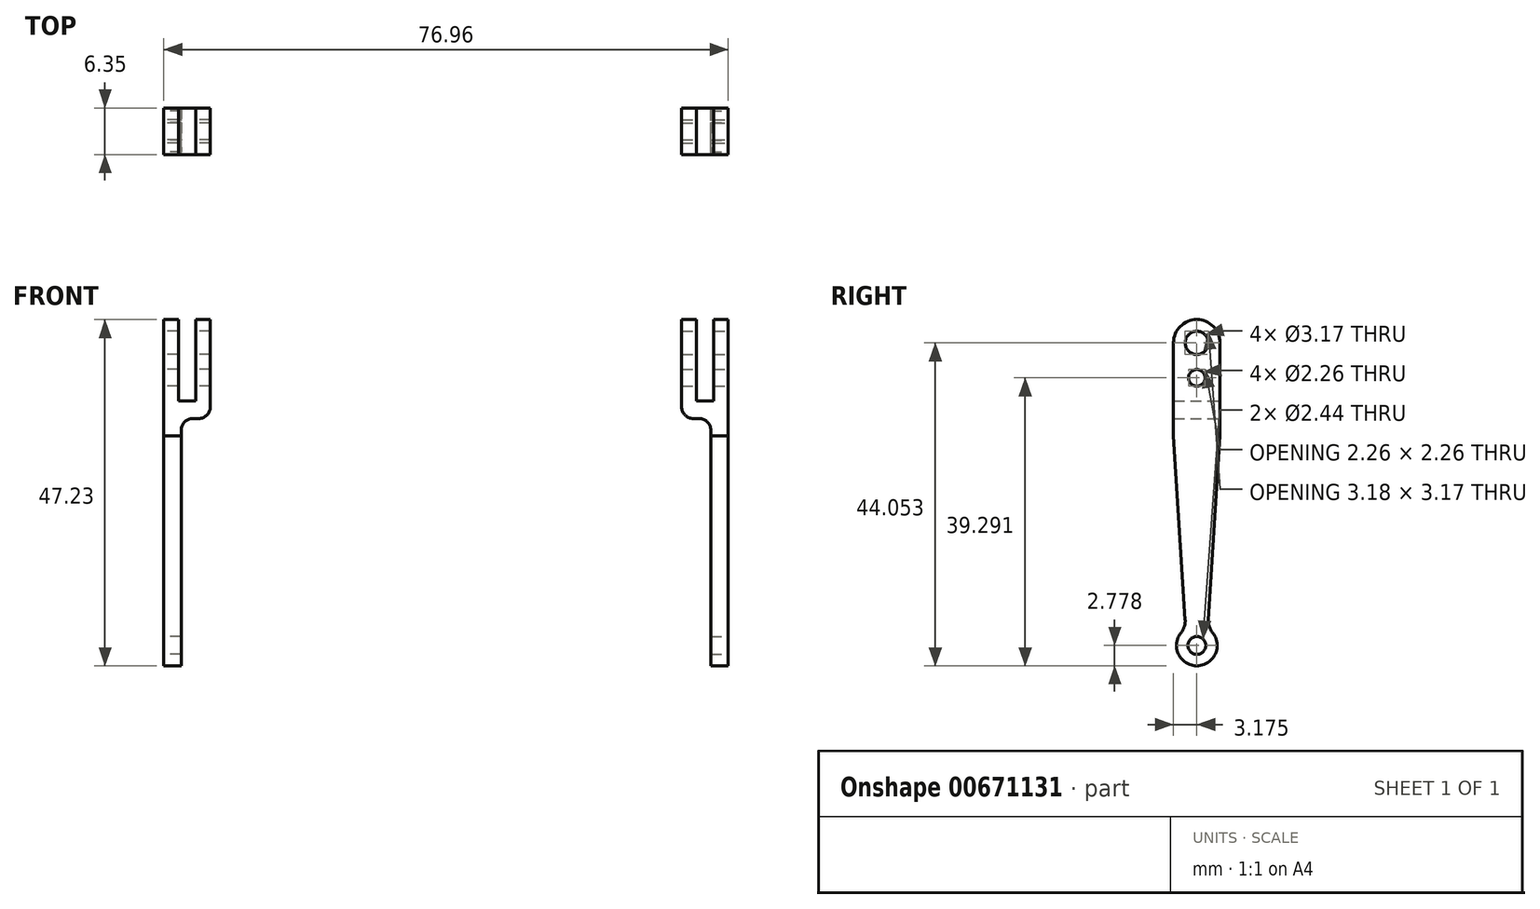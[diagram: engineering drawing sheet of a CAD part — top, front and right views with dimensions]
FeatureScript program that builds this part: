
annotation { "Feature Type Name" : "Feature", "Feature Type Description" : "" }
export const myFeature = defineFeature(function(context is Context, id is Id, definition is map)
    precondition{}
    {
        {
            var Q0;
            Q0=qCreatedBy(makeId("Front.planeOp"),FACE);
            var sketch = newSketch(context, id + "F0", { "sketchPlane" : qUnion([Q0])});
            skLineSegment(sketch, "E0", {"start": v(38.48, 4.76) * mm, "end": v(38.48, 51.99) * mm});
            skLineSegment(sketch, "E1", {"start": v(38.48, 51.99) * mm, "end": v(36.5, 51.99) * mm});
            skLineSegment(sketch, "E2", {"start": v(36.5, 51.99) * mm, "end": v(36.5, 40.88) * mm});
            skLineSegment(sketch, "E3", {"start": v(36.5, 40.88) * mm, "end": v(34.12, 40.88) * mm});
            skLineSegment(sketch, "E4", {"start": v(34.12, 40.88) * mm, "end": v(34.12, 51.99) * mm});
            skLineSegment(sketch, "E5", {"start": v(34.12, 51.99) * mm, "end": v(32.13, 51.99) * mm});
            skLineSegment(sketch, "E6", {"start": v(32.13, 51.99) * mm, "end": v(32.13, 38.5) * mm});
            skLineSegment(sketch, "E7", {"start": v(32.13, 38.5) * mm, "end": v(36.1, 38.5) * mm});
            skLineSegment(sketch, "E8", {"start": v(36.1, 38.5) * mm, "end": v(36.1, 4.76) * mm});
            skLineSegment(sketch, "E9", {"start": v(36.1, 4.76) * mm, "end": v(38.48, 4.76) * mm});
            skSolve(sketch);
        }
        {
            var Q0;
            Q0=qSketchRegion(id+"F0",true);
            extrude(context, id + "F1", {"entities" : qUnion([Q0]), "depth" : 6.35 * mm});
        }
        {
            var Q0;
            Q0=makeQuery(id+"F1.opExtrude","SWEPT_EDGE",EDGE,{"disambiguationData":[OSD([sQuery(id+"F0.wireOp",EDGE,"E7"),sQuery(id+"F0.wireOp",EDGE,"E8")])]});
            var Q1;
            Q1=makeQuery(id+"F1.opExtrude","SWEPT_EDGE",EDGE,{"disambiguationData":[OSD([sQuery(id+"F0.wireOp",EDGE,"E6"),sQuery(id+"F0.wireOp",EDGE,"E7")])]});
            fillet(context, id + "F2", {"entities" : qUnion([Q0, Q1]), "radius" : 1.59 * mm, "tangentPropagation" : true, "allowEdgeOverflow" : false});
        }
        {
            var Q0;
            Q0=makeQuery(id+"F1.opExtrude","CAP_EDGE",EDGE,{"disambiguationData":[OSD([sQuery(id+"F0.wireOp",EDGE,"E5")])],"isStart":false});
            var Q1;
            Q1=makeQuery(id+"F1.opExtrude","CAP_EDGE",EDGE,{"disambiguationData":[OSD([sQuery(id+"F0.wireOp",EDGE,"E5")])],"isStart":true});
            var Q2;
            Q2=makeQuery(id+"F1.opExtrude","CAP_EDGE",EDGE,{"disambiguationData":[OSD([sQuery(id+"F0.wireOp",EDGE,"E1")])],"isStart":true});
            var Q3;
            Q3=makeQuery(id+"F1.opExtrude","CAP_EDGE",EDGE,{"disambiguationData":[OSD([sQuery(id+"F0.wireOp",EDGE,"E1")])],"isStart":false});
            fillet(context, id + "F3", {"entities" : qUnion([Q0, Q1, Q2, Q3]), "radius" : 3.17 * mm, "tangentPropagation" : true, "allowEdgeOverflow" : false});
        }
        {
            var Q0;
            Q0=makeQuery(id+"F1.opExtrude","SWEPT_FACE",FACE,{"disambiguationData":[OSD([sQuery(id+"F0.wireOp",EDGE,"E0")])]});
            var sketch = newSketch(context, id + "F4", { "sketchPlane" : qUnion([Q0])});
            skPoint(sketch, "E10", {"position": v(-3.18, 48.81) * mm});
            skPoint(sketch, "E11", {"position": v(-3.18, 44.05) * mm});
            skSolve(sketch);
        }
        {
            var Q0;
            Q0=sQuery(id+"F4.wireOp",VERTEX,"E10");
            var Q1;
            Q1=makeQuery(id+"F1.opExtrude","SWEPT_BODY",BODY,{"disambiguationData":[OSD([sQuery(id+"F0.wireOp",EDGE,"E0"),sQuery(id+"F0.wireOp",EDGE,"E1"),sQuery(id+"F0.wireOp",EDGE,"E2"),sQuery(id+"F0.wireOp",EDGE,"E3"),sQuery(id+"F0.wireOp",EDGE,"E4"),sQuery(id+"F0.wireOp",EDGE,"E5"),sQuery(id+"F0.wireOp",EDGE,"E6"),sQuery(id+"F0.wireOp",EDGE,"E7"),sQuery(id+"F0.wireOp",EDGE,"E8"),sQuery(id+"F0.wireOp",EDGE,"E9")])]});
            hole(context, id + "F5", {"style" : HoleStyle.SIMPLE, "endStyle" : HoleEndStyle.THROUGH, "holeDiameter" : 3.17 * mm, "tappedDepth" : 12.7 * mm, "tapClearance" : 3, "locations" : qUnion([Q0]), "scope" : qUnion([Q1])});
        }
        {
            var Q0;
            Q0=makeQuery(id+"F1.opExtrude","SWEPT_FACE",FACE,{"disambiguationData":[OSD([sQuery(id+"F0.wireOp",EDGE,"E0")])]});
            var sketch = newSketch(context, id + "F6", { "sketchPlane" : qUnion([Q0])});
            skPoint(sketch, "E12", {"position": v(-3.18, 44.05) * mm});
            skSolve(sketch);
        }
        {
            var Q0;
            Q0=sQuery(id+"F6.wireOp",VERTEX,"E12");
            var Q1;
            Q1=makeQuery(id+"F1.opExtrude","SWEPT_BODY",BODY,{"disambiguationData":[OSD([sQuery(id+"F0.wireOp",EDGE,"E0"),sQuery(id+"F0.wireOp",EDGE,"E1"),sQuery(id+"F0.wireOp",EDGE,"E2"),sQuery(id+"F0.wireOp",EDGE,"E3"),sQuery(id+"F0.wireOp",EDGE,"E4"),sQuery(id+"F0.wireOp",EDGE,"E5"),sQuery(id+"F0.wireOp",EDGE,"E6"),sQuery(id+"F0.wireOp",EDGE,"E7"),sQuery(id+"F0.wireOp",EDGE,"E8"),sQuery(id+"F0.wireOp",EDGE,"E9")])]});
            hole(context, id + "F7", {"style" : HoleStyle.SIMPLE, "endStyle" : HoleEndStyle.THROUGH, "holeDiameter" : 2.26 * mm, "tappedDepth" : 12.7 * mm, "tapClearance" : 3, "locations" : qUnion([Q0]), "scope" : qUnion([Q1])});
        }
        {
            var Q0;
            Q0=makeQuery(id+"F1.opExtrude","SWEPT_FACE",FACE,{"disambiguationData":[OSD([sQuery(id+"F0.wireOp",EDGE,"E0")])]});
            var sketch = newSketch(context, id + "F8", { "sketchPlane" : qUnion([Q0])});
            skCircle(sketch, "E13", {"center": v(-3.18, 7.54) * mm, "radius": 1.22 * mm});
            skCircle(sketch, "E14", {"center": v(-3.18, 7.54) * mm, "radius": 2.78 * mm});
            skLineSegment(sketch, "E15", {"start": v(-6.35, 36.11) * mm, "end": v(0, 36.11) * mm});
            skLineSegment(sketch, "E16", {"start": v(-6.35, 11.06) * mm, "end": v(0, 11.06) * mm});
            skLineSegment(sketch, "E17", {"start": v(-6.35, 36.11) * mm, "end": v(-4.76, 11.06) * mm});
            skLineSegment(sketch, "E18", {"start": v(0, 36.11) * mm, "end": v(-1.59, 11.06) * mm});
            skArc(sketch, "E19", {"start": v(-5.33, 9.3) * mm, "mid": v(-4.88, 10.12) * mm, "end": v(-4.76, 11.06) * mm});
            skArc(sketch, "E20", {"start": v(-1.59, 11.06) * mm, "mid": v(-1.47, 10.12) * mm, "end": v(-1.02, 9.3) * mm});
            skSolve(sketch);
        }
        {
            var Q0;
            {var subQ3=sQuery(id+"F8.wireOp",EDGE,"E17");Q0=makeQuery(id+"F8.imprint","IMPRINT",FACE,{"disambiguationData":[TD([[makeQuery(id+"F8.imprint","IMPRINT",EDGE,{"derivedFrom":subQ3}),-1.0]])]});}
            var Q1;
            {var subQ8=sQuery(id+"F8.wireOp",EDGE,"E19");Q1=makeQuery(id+"F8.imprint","IMPRINT",FACE,{"disambiguationData":[TD([[makeQuery(id+"F8.imprint","IMPRINT",EDGE,{"derivedFrom":subQ8}),1.0]])]});}
            var Q2;
            Q2=makeQuery(id+"F8.imprint","IMPRINT",FACE,{"disambiguationData":[TD([[makeQuery(id+"F8.imprint","IMPRINT",EDGE,{"derivedFrom":sQuery(id+"F8.wireOp",EDGE,"E13")}),1.0]])]});
            var Q3;
            {var subQ8=sQuery(id+"F8.wireOp",EDGE,"E20");Q3=makeQuery(id+"F8.imprint","IMPRINT",FACE,{"disambiguationData":[TD([[makeQuery(id+"F8.imprint","IMPRINT",EDGE,{"derivedFrom":subQ8}),1.0]])]});}
            var Q4;
            {var subQ3=sQuery(id+"F8.wireOp",EDGE,"E18");Q4=makeQuery(id+"F8.imprint","IMPRINT",FACE,{"disambiguationData":[TD([[makeQuery(id+"F8.imprint","IMPRINT",EDGE,{"derivedFrom":subQ3}),1.0]])]});}
            extrude(context, id + "F9", {"entities" : qUnion([Q0, Q1, Q2, Q3, Q4]), "operationType" : NewBodyOperationType.REMOVE, "oppositeDirection" : true, "depth" : 25.4 * mm});
        }
        {
            var Q0;
            Q0=qCreatedBy(makeId("Right.planeOp"),FACE);
            var sketch = newSketch(context, id + "F10", { "sketchPlane" : qUnion([Q0])});
            skLineSegment(sketch, "E21.bottom", {"start": v(0, 46.47) * mm, "end": v(29.77, 46.47) * mm});
            skLineSegment(sketch, "E21.top", {"start": v(0, 19.75) * mm, "end": v(29.77, 19.75) * mm});
            skLineSegment(sketch, "E21.left", {"start": v(0, 46.47) * mm, "end": v(0, 19.75) * mm});
            skLineSegment(sketch, "E21.right", {"start": v(29.77, 46.47) * mm, "end": v(29.77, 19.75) * mm});
            skSolve(sketch);
        }
        {
            var Q0;
            Q0=makeQuery(id+"F1.opExtrude","SWEPT_BODY",BODY,{"disambiguationData":[OSD([sQuery(id+"F0.wireOp",EDGE,"E0"),sQuery(id+"F0.wireOp",EDGE,"E1"),sQuery(id+"F0.wireOp",EDGE,"E2"),sQuery(id+"F0.wireOp",EDGE,"E3"),sQuery(id+"F0.wireOp",EDGE,"E4"),sQuery(id+"F0.wireOp",EDGE,"E5"),sQuery(id+"F0.wireOp",EDGE,"E6"),sQuery(id+"F0.wireOp",EDGE,"E7"),sQuery(id+"F0.wireOp",EDGE,"E8"),sQuery(id+"F0.wireOp",EDGE,"E9")])]});
            var Q1;
            Q1=makeQuery(id+"F10.imprint","IMPRINT",FACE,{"disambiguationData":[TD([[makeQuery(id+"F10.imprint","IMPRINT",EDGE,{"derivedFrom":sQuery(id+"F10.wireOp",EDGE,"E21.bottom")}),-1.0]])]});
            mirror(context, id + "F11", {"entities" : qUnion([Q0]), "mirrorPlane" : qUnion([Q1])});
        }
    });
